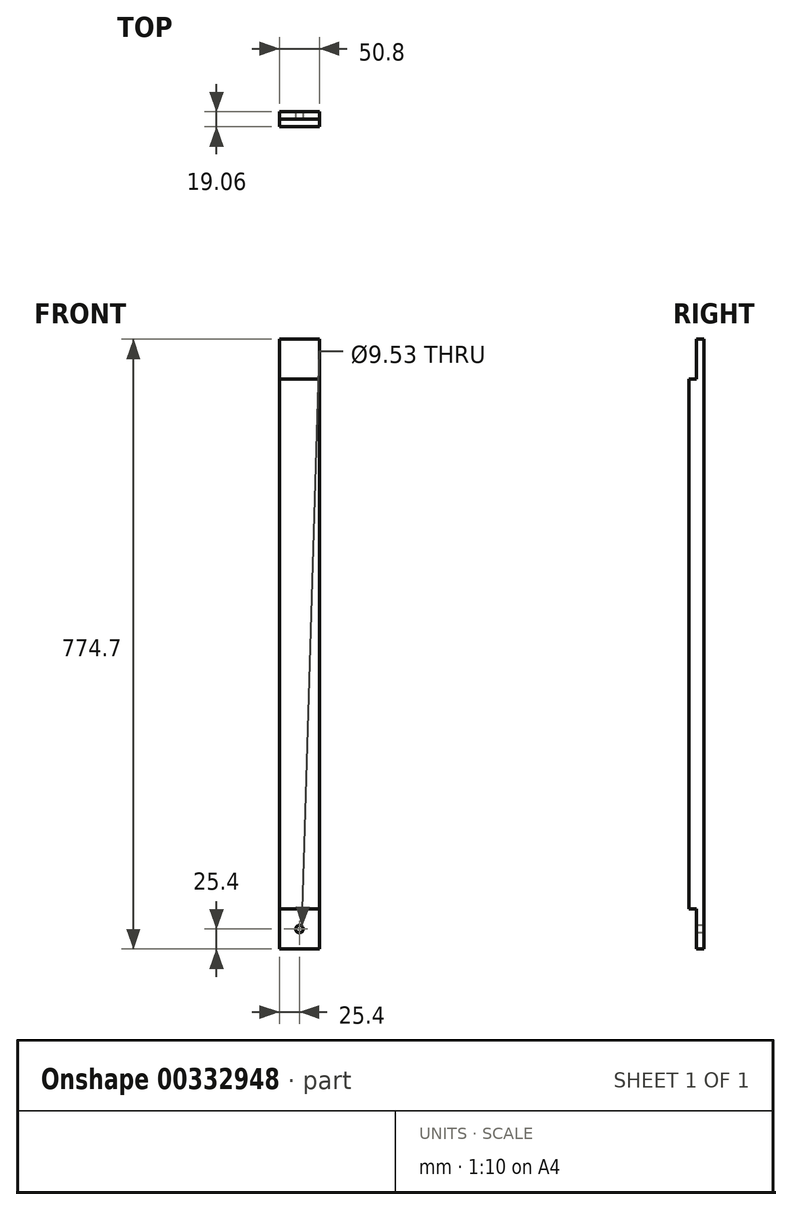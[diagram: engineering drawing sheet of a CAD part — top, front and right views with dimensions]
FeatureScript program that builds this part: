
annotation { "Feature Type Name" : "Feature", "Feature Type Description" : "" }
export const myFeature = defineFeature(function(context is Context, id is Id, definition is map)
    precondition{}
    {
        {
            var Q0;
            Q0=qCreatedBy(makeId("Top.planeOp"),FACE);
            var sketch = newSketch(context, id + "F0", { "sketchPlane" : qUnion([Q0])});
            skLineSegment(sketch, "E0.bottom", {"start": v(25.4, 9.53) * mm, "end": v(-25.4, 9.53) * mm});
            skLineSegment(sketch, "E0.top", {"start": v(25.4, -9.53) * mm, "end": v(-25.4, -9.53) * mm});
            skLineSegment(sketch, "E0.left", {"start": v(25.4, 9.53) * mm, "end": v(25.4, -9.52) * mm});
            skLineSegment(sketch, "E0.right", {"start": v(-25.4, 9.53) * mm, "end": v(-25.4, -9.53) * mm});
            skPoint(sketch, "E0.middle", {"position": v(0, 0) * mm});
            skSolve(sketch);
        }
        {
            var Q0;
            Q0=makeQuery(id+"F0.imprint","IMPRINT",FACE,{"disambiguationData":[TD([[makeQuery(id+"F0.imprint","IMPRINT",EDGE,{"derivedFrom":sQuery(id+"F0.wireOp",EDGE,"E0.bottom")}),1.0]])]});
            var Q1;
            Q1=qSketchRegion(id+"F2",true);
            extrude(context, id + "F1", {"entities" : qUnion([Q0, Q1]), "depth" : 774.7 * mm});
        }
        {
            var Q0;
            Q0=qCreatedBy(makeId("Front.planeOp"),FACE);
            var sketch = newSketch(context, id + "F2", { "sketchPlane" : qUnion([Q0])});
            skLineSegment(sketch, "E1.bottom", {"start": v(-38.77, 0) * mm, "end": v(83.66, 0) * mm});
            skLineSegment(sketch, "E1.top", {"start": v(-38.77, 50.8) * mm, "end": v(83.66, 50.8) * mm});
            skLineSegment(sketch, "E1.left", {"start": v(-38.77, 0) * mm, "end": v(-38.77, 50.8) * mm});
            skLineSegment(sketch, "E1.right", {"start": v(83.66, 0) * mm, "end": v(83.66, 50.8) * mm});
            skLineSegment(sketch, "E2.bottom", {"start": v(-210.36, 723.9) * mm, "end": v(132.8, 723.9) * mm});
            skLineSegment(sketch, "E2.top", {"start": v(-210.36, 774.7) * mm, "end": v(132.8, 774.7) * mm});
            skLineSegment(sketch, "E2.left", {"start": v(-210.36, 723.9) * mm, "end": v(-210.36, 774.7) * mm});
            skLineSegment(sketch, "E2.right", {"start": v(132.8, 723.9) * mm, "end": v(132.8, 774.7) * mm});
            skSolve(sketch);
        }
        {
            var Q0;
            Q0=qSketchRegion(id+"F2",true);
            extrude(context, id + "F3", {"entities" : qUnion([Q0]), "operationType" : NewBodyOperationType.REMOVE, "depth" : 25.4 * mm});
        }
        {
            var Q0;
            Q0=qCreatedBy(makeId("Front.planeOp"),FACE);
            var sketch = newSketch(context, id + "F4", { "sketchPlane" : qUnion([Q0])});
            skCircle(sketch, "E3", {"center": v(0, 25.4) * mm, "radius": 4.76 * mm});
            skSolve(sketch);
        }
        {
            var Q0;
            Q0=qSketchRegion(id+"F4",true);
            extrude(context, id + "F5", {"entities" : qUnion([Q0]), "operationType" : NewBodyOperationType.REMOVE, "oppositeDirection" : true, "depth" : 25.4 * mm});
        }
    });
